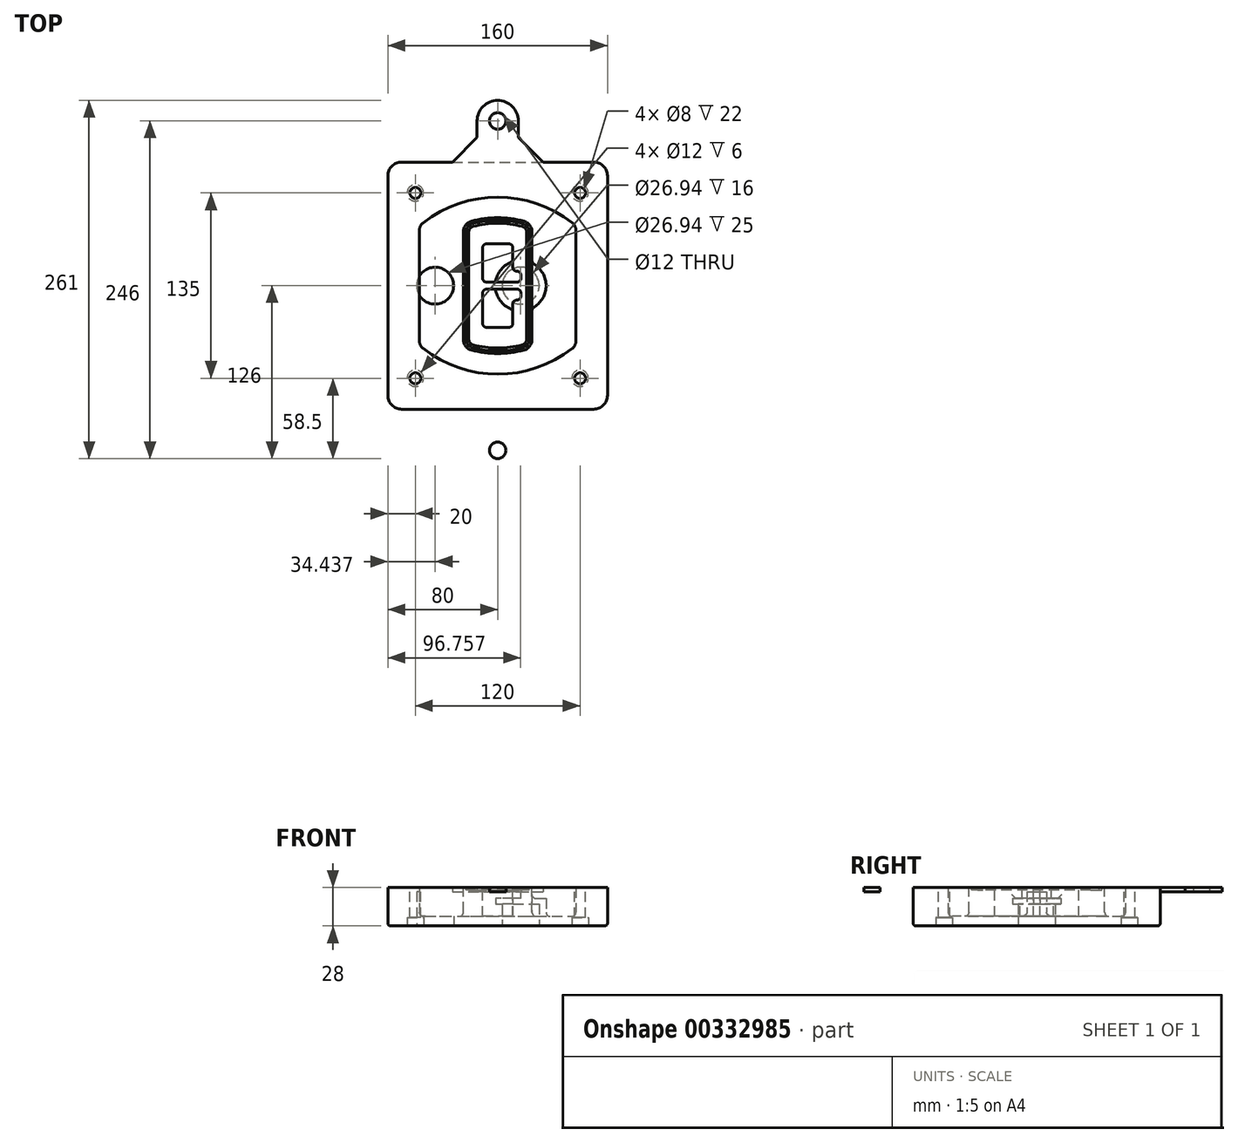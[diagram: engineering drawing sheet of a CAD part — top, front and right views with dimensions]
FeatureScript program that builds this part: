
annotation { "Feature Type Name" : "Feature", "Feature Type Description" : "" }
export const myFeature = defineFeature(function(context is Context, id is Id, definition is map)
    precondition{}
    {
        {
            var Q0;
            Q0=qCreatedBy(makeId("Top.planeOp"),FACE);
            var sketch = newSketch(context, id + "F0", { "sketchPlane" : qUnion([Q0])});
            skPoint(sketch, "E0.rect.middle", {"position": v(0, 0) * mm});
            skLineSegment(sketch, "E1.bottom", {"start": v(-70, -90) * mm, "end": v(70, -90) * mm});
            skLineSegment(sketch, "E1.top", {"start": v(-70, 90) * mm, "end": v(70, 90) * mm});
            skLineSegment(sketch, "E1.left", {"start": v(-80, -80) * mm, "end": v(-80, 80) * mm});
            skLineSegment(sketch, "E1.right", {"start": v(80, -80) * mm, "end": v(80, 80) * mm});
            skLineSegment(sketch, "E2", {"start": v(-80, 90) * mm, "end": v(80, -90) * mm, "construction": true});
            skLineSegment(sketch, "E3", {"start": v(80, 90) * mm, "end": v(-80, -90) * mm, "construction": true});
            skCircle(sketch, "E4", {"center": v(-60, 67.5) * mm, "radius": 4 * mm});
            skCircle(sketch, "E5", {"center": v(60, 67.5) * mm, "radius": 4 * mm});
            skCircle(sketch, "E6", {"center": v(60, -67.5) * mm, "radius": 4 * mm});
            skCircle(sketch, "E7", {"center": v(-60, -67.5) * mm, "radius": 4 * mm});
            skLineSegment(sketch, "E8", {"start": v(-60, 67.5) * mm, "end": v(60, 67.5) * mm, "construction": true});
            skLineSegment(sketch, "E9", {"start": v(60, 67.5) * mm, "end": v(60, -67.5) * mm, "construction": true});
            skLineSegment(sketch, "E10", {"start": v(60, -67.5) * mm, "end": v(-60, -67.5) * mm, "construction": true});
            skLineSegment(sketch, "E11", {"start": v(-60, -67.5) * mm, "end": v(-60, 67.5) * mm, "construction": true});
            skLineSegment(sketch, "E12", {"start": v(-60, 40.3) * mm, "end": v(-60, -40.3) * mm});
            skLineSegment(sketch, "E13", {"start": v(60, 40.3) * mm, "end": v(60, -40.3) * mm});
            skArc(sketch, "E14", {"start": v(56.15, 48.18) * mm, "mid": v(0, 67.5) * mm, "end": v(-56.15, 48.18) * mm});
            skArc(sketch, "E15", {"start": v(-56.15, -48.18) * mm, "mid": v(0, -67.5) * mm, "end": v(56.15, -48.18) * mm});
            skLineSegment(sketch, "E16", {"start": v(-60, 0) * mm, "end": v(60, 0) * mm, "construction": true});
            skPoint(sketch, "E17.visualSharp", {"position": v(-60, -45) * mm});
            skArc(sketch, "E17.filletArc", {"start": v(-60, -40.3) * mm, "mid": v(-58.99, -44.68) * mm, "end": v(-56.15, -48.18) * mm});
            skPoint(sketch, "E18.visualSharp", {"position": v(-60, 45) * mm});
            skArc(sketch, "E18.filletArc", {"start": v(-56.15, 48.18) * mm, "mid": v(-58.99, 44.68) * mm, "end": v(-60, 40.3) * mm});
            skPoint(sketch, "E19.visualSharp", {"position": v(60, 45) * mm});
            skArc(sketch, "E19.filletArc", {"start": v(60, 40.3) * mm, "mid": v(58.99, 44.68) * mm, "end": v(56.15, 48.18) * mm});
            skPoint(sketch, "E20.visualSharp", {"position": v(60, -45) * mm});
            skArc(sketch, "E20.filletArc", {"start": v(56.15, -48.18) * mm, "mid": v(58.99, -44.68) * mm, "end": v(60, -40.3) * mm});
            skPoint(sketch, "E21.visualSharp", {"position": v(-80, 90) * mm});
            skArc(sketch, "E21.filletArc", {"start": v(-70, 90) * mm, "mid": v(-77.07, 87.07) * mm, "end": v(-80, 80) * mm});
            skPoint(sketch, "E22.visualSharp", {"position": v(80, 90) * mm});
            skArc(sketch, "E22.filletArc", {"start": v(80, 80) * mm, "mid": v(77.07, 87.07) * mm, "end": v(70, 90) * mm});
            skPoint(sketch, "E23.visualSharp", {"position": v(80, -90) * mm});
            skArc(sketch, "E23.filletArc", {"start": v(70, -90) * mm, "mid": v(77.07, -87.07) * mm, "end": v(80, -80) * mm});
            skPoint(sketch, "E24.visualSharp", {"position": v(-80, -90) * mm});
            skArc(sketch, "E24.filletArc", {"start": v(-80, -80) * mm, "mid": v(-77.07, -87.07) * mm, "end": v(-70, -90) * mm});
            skArc(sketch, "E25.0", {"start": v(57, 40.3) * mm, "mid": v(56.3, 43.36) * mm, "end": v(54.3, 45.81) * mm});
            skLineSegment(sketch, "E25.1", {"start": v(57, 40.3) * mm, "end": v(57, -40.3) * mm});
            skArc(sketch, "E25.2", {"start": v(54.3, -45.81) * mm, "mid": v(56.3, -43.36) * mm, "end": v(57, -40.3) * mm});
            skArc(sketch, "E25.3", {"start": v(-54.3, -45.81) * mm, "mid": v(0, -64.5) * mm, "end": v(54.3, -45.81) * mm});
            skArc(sketch, "E25.4", {"start": v(-57, -40.3) * mm, "mid": v(-56.3, -43.36) * mm, "end": v(-54.3, -45.81) * mm});
            skArc(sketch, "E25.5", {"start": v(54.3, 45.81) * mm, "mid": v(0, 64.5) * mm, "end": v(-54.3, 45.81) * mm});
            skLineSegment(sketch, "E25.6", {"start": v(-57, 40.3) * mm, "end": v(-57, -40.3) * mm});
            skArc(sketch, "E25.7", {"start": v(-54.3, 45.81) * mm, "mid": v(-56.3, 43.36) * mm, "end": v(-57, 40.3) * mm});
            skArc(sketch, "E26.0", {"start": v(-58.62, 51.33) * mm, "mid": v(-62.58, 46.43) * mm, "end": v(-64, 40.3) * mm});
            skArc(sketch, "E26.1", {"start": v(58.62, 51.33) * mm, "mid": v(0, 71.5) * mm, "end": v(-58.62, 51.33) * mm});
            skArc(sketch, "E26.2", {"start": v(64, 40.3) * mm, "mid": v(62.58, 46.43) * mm, "end": v(58.62, 51.33) * mm});
            skLineSegment(sketch, "E26.3", {"start": v(64, 40.3) * mm, "end": v(64, -40.3) * mm});
            skArc(sketch, "E26.4", {"start": v(58.62, -51.33) * mm, "mid": v(62.58, -46.43) * mm, "end": v(64, -40.3) * mm});
            skLineSegment(sketch, "E26.5", {"start": v(-64, 40.3) * mm, "end": v(-64, -40.3) * mm});
            skArc(sketch, "E26.6", {"start": v(-58.62, -51.33) * mm, "mid": v(0, -71.5) * mm, "end": v(58.62, -51.33) * mm});
            skArc(sketch, "E26.7", {"start": v(-64, -40.3) * mm, "mid": v(-62.58, -46.43) * mm, "end": v(-58.62, -51.33) * mm});
            skSolve(sketch);
        }
        {
            var Q0;
            Q0=makeQuery(id+"F0.imprint","IMPRINT",FACE,{"disambiguationData":[TD([[makeQuery(id+"F0.imprint","IMPRINT",EDGE,{"derivedFrom":sQuery(id+"F0.wireOp",EDGE,"E1.bottom")}),1.0]])]});
            var Q1;
            Q1=makeQuery(id+"F0.imprint","IMPRINT",FACE,{"disambiguationData":[TD([[makeQuery(id+"F0.imprint","IMPRINT",EDGE,{"derivedFrom":sQuery(id+"F0.wireOp",EDGE,"E12")}),1.0]])]});
            var Q2;
            Q2=makeQuery(id+"F0.imprint","IMPRINT",FACE,{"disambiguationData":[TD([[makeQuery(id+"F0.imprint","IMPRINT",EDGE,{"derivedFrom":sQuery(id+"F0.wireOp",EDGE,"E25.0")}),1.0]])]});
            var Q3;
            Q3=makeQuery(id+"F0.imprint","IMPRINT",FACE,{"disambiguationData":[TD([[makeQuery(id+"F0.imprint","IMPRINT",EDGE,{"derivedFrom":sQuery(id+"F0.wireOp",EDGE,"E12")}),-1.0]])]});
            extrude(context, id + "F1", {"entities" : qUnion([Q0, Q1, Q2, Q3]), "oppositeDirection" : true, "depth" : 25 * mm});
        }
        {
            var Q0;
            Q0=makeQuery(id+"F0.imprint","IMPRINT",FACE,{"disambiguationData":[TD([[makeQuery(id+"F0.imprint","IMPRINT",EDGE,{"derivedFrom":sQuery(id+"F0.wireOp",EDGE,"E12")}),1.0]])]});
            extrude(context, id + "F2", {"entities" : qUnion([Q0]), "operationType" : NewBodyOperationType.ADD, "depth" : 3 * mm});
        }
        {
            var Q0;
            Q0=makeQuery(id+"F0.imprint","IMPRINT",FACE,{"disambiguationData":[TD([[makeQuery(id+"F0.imprint","IMPRINT",EDGE,{"derivedFrom":sQuery(id+"F0.wireOp",EDGE,"E25.0")}),1.0]])]});
            extrude(context, id + "F3", {"entities" : qUnion([Q0]), "operationType" : NewBodyOperationType.REMOVE, "oppositeDirection" : true, "depth" : 18 * mm});
        }
        {
            var Q0;
            Q0=makeQuery(id+"F2.opExtrude","CAP_FACE",FACE,{"disambiguationData":[OSD([sQuery(id+"F0.wireOp",EDGE,"E12"),sQuery(id+"F0.wireOp",EDGE,"E13"),sQuery(id+"F0.wireOp",EDGE,"E14"),sQuery(id+"F0.wireOp",EDGE,"E15"),sQuery(id+"F0.wireOp",EDGE,"E17.filletArc"),sQuery(id+"F0.wireOp",EDGE,"E18.filletArc"),sQuery(id+"F0.wireOp",EDGE,"E19.filletArc"),sQuery(id+"F0.wireOp",EDGE,"E20.filletArc"),sQuery(id+"F0.wireOp",EDGE,"E25.0"),sQuery(id+"F0.wireOp",EDGE,"E25.1"),sQuery(id+"F0.wireOp",EDGE,"E25.2"),sQuery(id+"F0.wireOp",EDGE,"E25.3"),sQuery(id+"F0.wireOp",EDGE,"E25.4"),sQuery(id+"F0.wireOp",EDGE,"E25.5"),sQuery(id+"F0.wireOp",EDGE,"E25.6"),sQuery(id+"F0.wireOp",EDGE,"E25.7")])],"isStart":false});
            var sketch = newSketch(context, id + "F4", { "sketchPlane" : qUnion([Q0])});
            skArc(sketch, "E27.0", {"start": v(-19.08, -46.97) * mm, "mid": v(0, -49.5) * mm, "end": v(19.08, -46.97) * mm});
            skArc(sketch, "E28.0", {"start": v(19.08, 46.97) * mm, "mid": v(0, 49.5) * mm, "end": v(-19.08, 46.97) * mm});
            skLineSegment(sketch, "E29", {"start": v(-25, 39.25) * mm, "end": v(-25, -39.25) * mm});
            skLineSegment(sketch, "E30", {"start": v(25, 39.25) * mm, "end": v(25, -39.25) * mm});
            skLineSegment(sketch, "E31", {"start": v(-25, 45.1) * mm, "end": v(25, 45.1) * mm, "construction": true});
            skLineSegment(sketch, "E32", {"start": v(-25, -45.1) * mm, "end": v(25, -45.1) * mm, "construction": true});
            skPoint(sketch, "E33.visualSharp", {"position": v(-25, 45.1) * mm});
            skArc(sketch, "E33.filletArc", {"start": v(-19.08, 46.97) * mm, "mid": v(-23.35, 44.11) * mm, "end": v(-25, 39.25) * mm});
            skPoint(sketch, "E34.visualSharp", {"position": v(25, 45.1) * mm});
            skArc(sketch, "E34.filletArc", {"start": v(25, 39.25) * mm, "mid": v(23.35, 44.11) * mm, "end": v(19.08, 46.97) * mm});
            skPoint(sketch, "E35.visualSharp", {"position": v(25, -45.1) * mm});
            skArc(sketch, "E35.filletArc", {"start": v(19.08, -46.97) * mm, "mid": v(23.35, -44.11) * mm, "end": v(25, -39.25) * mm});
            skPoint(sketch, "E36.visualSharp", {"position": v(-25, -45.1) * mm});
            skArc(sketch, "E36.filletArc", {"start": v(-25, -39.25) * mm, "mid": v(-23.35, -44.11) * mm, "end": v(-19.08, -46.97) * mm});
            skArc(sketch, "E37.0", {"start": v(54.3, 45.81) * mm, "mid": v(0, 64.5) * mm, "end": v(-54.3, 45.81) * mm});
            skArc(sketch, "E37.1", {"start": v(-54.3, 45.81) * mm, "mid": v(-56.3, 43.36) * mm, "end": v(-57, 40.3) * mm});
            skLineSegment(sketch, "E37.2", {"start": v(-57, 40.3) * mm, "end": v(-57, -40.3) * mm});
            skArc(sketch, "E37.3", {"start": v(-57, -40.3) * mm, "mid": v(-56.3, -43.36) * mm, "end": v(-54.3, -45.81) * mm});
            skArc(sketch, "E37.4", {"start": v(-54.3, -45.81) * mm, "mid": v(0, -64.5) * mm, "end": v(54.3, -45.81) * mm});
            skArc(sketch, "E37.5", {"start": v(54.3, -45.81) * mm, "mid": v(56.3, -43.36) * mm, "end": v(57, -40.3) * mm});
            skLineSegment(sketch, "E37.6", {"start": v(57, 40.3) * mm, "end": v(57, -40.3) * mm});
            skArc(sketch, "E37.7", {"start": v(57, 40.3) * mm, "mid": v(56.3, 43.36) * mm, "end": v(54.3, 45.81) * mm});
            skLineSegment(sketch, "E38.0", {"start": v(23, 39.25) * mm, "end": v(23, -39.25) * mm});
            skArc(sketch, "E38.1", {"start": v(18.56, -45.04) * mm, "mid": v(21.76, -42.9) * mm, "end": v(23, -39.25) * mm});
            skArc(sketch, "E38.2", {"start": v(-18.56, -45.04) * mm, "mid": v(0, -47.5) * mm, "end": v(18.56, -45.04) * mm});
            skArc(sketch, "E38.3", {"start": v(-23, -39.25) * mm, "mid": v(-21.76, -42.9) * mm, "end": v(-18.56, -45.04) * mm});
            skLineSegment(sketch, "E38.4", {"start": v(-23, 39.25) * mm, "end": v(-23, -39.25) * mm});
            skArc(sketch, "E38.5", {"start": v(23, 39.25) * mm, "mid": v(21.76, 42.9) * mm, "end": v(18.56, 45.04) * mm});
            skArc(sketch, "E38.6", {"start": v(-18.56, 45.04) * mm, "mid": v(-21.76, 42.9) * mm, "end": v(-23, 39.25) * mm});
            skArc(sketch, "E38.7", {"start": v(18.56, 45.04) * mm, "mid": v(0, 47.5) * mm, "end": v(-18.56, 45.04) * mm});
            skArc(sketch, "E39.0", {"start": v(21, 39.25) * mm, "mid": v(20.18, 41.68) * mm, "end": v(18.04, 43.1) * mm});
            skLineSegment(sketch, "E39.1", {"start": v(21, 39.25) * mm, "end": v(21, -39.25) * mm});
            skArc(sketch, "E39.2", {"start": v(18.04, -43.1) * mm, "mid": v(20.18, -41.68) * mm, "end": v(21, -39.25) * mm});
            skArc(sketch, "E39.3", {"start": v(-18.04, -43.1) * mm, "mid": v(0, -45.5) * mm, "end": v(18.04, -43.1) * mm});
            skArc(sketch, "E39.4", {"start": v(-21, -39.25) * mm, "mid": v(-20.18, -41.68) * mm, "end": v(-18.04, -43.1) * mm});
            skArc(sketch, "E39.5", {"start": v(18.04, 43.1) * mm, "mid": v(0, 45.5) * mm, "end": v(-18.04, 43.1) * mm});
            skLineSegment(sketch, "E39.6", {"start": v(-21, 39.25) * mm, "end": v(-21, -39.25) * mm});
            skArc(sketch, "E39.7", {"start": v(-18.04, 43.1) * mm, "mid": v(-20.18, 41.68) * mm, "end": v(-21, 39.25) * mm});
            skLineSegment(sketch, "E40", {"start": v(-25, 0) * mm, "end": v(25, 0) * mm, "construction": true});
            skLineSegment(sketch, "E41", {"start": v(-11, 5.5) * mm, "end": v(-11, 27.5) * mm});
            skLineSegment(sketch, "E42", {"start": v(-8, 30.5) * mm, "end": v(8, 30.5) * mm});
            skLineSegment(sketch, "E43", {"start": v(11, 27.5) * mm, "end": v(11, 13.5) * mm});
            skLineSegment(sketch, "E44", {"start": v(14, 10.5) * mm, "end": v(14, 10.5) * mm});
            skLineSegment(sketch, "E45", {"start": v(17, 7.5) * mm, "end": v(17, 5.5) * mm});
            skLineSegment(sketch, "E46", {"start": v(14, 2.5) * mm, "end": v(-8, 2.5) * mm});
            skPoint(sketch, "E47.visualSharp", {"position": v(-11, 30.5) * mm});
            skArc(sketch, "E47.filletArc", {"start": v(-8, 30.5) * mm, "mid": v(-10.12, 29.62) * mm, "end": v(-11, 27.5) * mm});
            skPoint(sketch, "E48.visualSharp", {"position": v(11, 30.5) * mm});
            skArc(sketch, "E48.filletArc", {"start": v(11, 27.5) * mm, "mid": v(10.12, 29.62) * mm, "end": v(8, 30.5) * mm});
            skPoint(sketch, "E49.visualSharp", {"position": v(11, 10.5) * mm});
            skArc(sketch, "E49.filletArc", {"start": v(11, 13.5) * mm, "mid": v(11.88, 11.38) * mm, "end": v(14, 10.5) * mm});
            skPoint(sketch, "E50.visualSharp", {"position": v(17, 10.5) * mm});
            skArc(sketch, "E50.filletArc", {"start": v(17, 7.5) * mm, "mid": v(16.12, 9.62) * mm, "end": v(14, 10.5) * mm});
            skPoint(sketch, "E51.visualSharp", {"position": v(17, 2.5) * mm});
            skArc(sketch, "E51.filletArc", {"start": v(14, 2.5) * mm, "mid": v(16.12, 3.38) * mm, "end": v(17, 5.5) * mm});
            skPoint(sketch, "E52.visualSharp", {"position": v(-11, 2.5) * mm});
            skArc(sketch, "E52.filletArc", {"start": v(-11, 5.5) * mm, "mid": v(-10.12, 3.38) * mm, "end": v(-8, 2.5) * mm});
            skLineSegment(sketch, "E53.0.MirrorCS", {"start": v(14, -2.5) * mm, "end": v(-8, -2.5) * mm});
            skArc(sketch, "E54.0.MirrorCS", {"start": v(-11, -5.5) * mm, "mid": v(-10.12, -3.38) * mm, "end": v(-8, -2.5) * mm});
            skLineSegment(sketch, "E55.0.MirrorCS", {"start": v(-11, -5.5) * mm, "end": v(-11, -27.5) * mm});
            skArc(sketch, "E56.0.MirrorCS", {"start": v(-8, -30.5) * mm, "mid": v(-10.12, -29.62) * mm, "end": v(-11, -27.5) * mm});
            skLineSegment(sketch, "E57.0.MirrorCS", {"start": v(-8, -30.5) * mm, "end": v(8, -30.5) * mm});
            skArc(sketch, "E58.0.MirrorCS", {"start": v(11, -27.5) * mm, "mid": v(10.12, -29.62) * mm, "end": v(8, -30.5) * mm});
            skLineSegment(sketch, "E59.0.MirrorCS", {"start": v(11, -27.5) * mm, "end": v(11, -13.5) * mm});
            skArc(sketch, "E60.0.MirrorCS", {"start": v(11, -13.5) * mm, "mid": v(11.88, -11.38) * mm, "end": v(14, -10.5) * mm});
            skArc(sketch, "E61.0.MirrorCS", {"start": v(17, -7.5) * mm, "mid": v(16.12, -9.62) * mm, "end": v(14, -10.5) * mm});
            skLineSegment(sketch, "E62.0.MirrorCS", {"start": v(17, -7.5) * mm, "end": v(17, -5.5) * mm});
            skArc(sketch, "E63.0.MirrorCS", {"start": v(14, -2.5) * mm, "mid": v(16.12, -3.38) * mm, "end": v(17, -5.5) * mm});
            skSolve(sketch);
        }
        {
            var Q0;
            Q0=makeQuery(id+"F4.imprint","IMPRINT",FACE,{"disambiguationData":[TD([[makeQuery(id+"F4.imprint","IMPRINT",EDGE,{"derivedFrom":sQuery(id+"F4.wireOp",EDGE,"E27.0")}),1.0]])]});
            var Q1;
            Q1=makeQuery(id+"F4.imprint","IMPRINT",FACE,{"disambiguationData":[TD([[makeQuery(id+"F4.imprint","IMPRINT",EDGE,{"derivedFrom":sQuery(id+"F4.wireOp",EDGE,"E38.0")}),-1.0]])]});
            var Q2;
            Q2=makeQuery(id+"F4.imprint","IMPRINT",FACE,{"disambiguationData":[TD([[makeQuery(id+"F4.imprint","IMPRINT",EDGE,{"derivedFrom":sQuery(id+"F4.wireOp",EDGE,"E39.0")}),1.0]])]});
            extrude(context, id + "F5", {"entities" : qUnion([Q0, Q1, Q2]), "operationType" : NewBodyOperationType.ADD, "endBound" : BoundingType.UP_TO_NEXT, "oppositeDirection" : true, "depth" : 25 * mm});
        }
        {
            var Q0;
            Q0=makeQuery(id+"F4.imprint","IMPRINT",FACE,{"disambiguationData":[TD([[makeQuery(id+"F4.imprint","IMPRINT",EDGE,{"derivedFrom":sQuery(id+"F4.wireOp",EDGE,"E38.0")}),-1.0]])]});
            extrude(context, id + "F6", {"entities" : qUnion([Q0]), "operationType" : NewBodyOperationType.REMOVE, "oppositeDirection" : true, "depth" : 2 * mm});
        }
        {
            var Q0;
            Q0=makeQuery(id+"F1.opExtrude","CAP_FACE",FACE,{"disambiguationData":[OSD([sQuery(id+"F0.wireOp",EDGE,"E1.bottom"),sQuery(id+"F0.wireOp",EDGE,"E1.top"),sQuery(id+"F0.wireOp",EDGE,"E1.left"),sQuery(id+"F0.wireOp",EDGE,"E1.right"),sQuery(id+"F0.wireOp",EDGE,"E4"),sQuery(id+"F0.wireOp",EDGE,"E5"),sQuery(id+"F0.wireOp",EDGE,"E6"),sQuery(id+"F0.wireOp",EDGE,"E7"),sQuery(id+"F0.wireOp",EDGE,"E21.filletArc"),sQuery(id+"F0.wireOp",EDGE,"E22.filletArc"),sQuery(id+"F0.wireOp",EDGE,"E23.filletArc"),sQuery(id+"F0.wireOp",EDGE,"E24.filletArc")])],"isStart":false});
            var sketch = newSketch(context, id + "F7", { "sketchPlane" : qUnion([Q0])});
            skCircle(sketch, "E64", {"center": v(16.76, 0) * mm, "radius": 13.47 * mm});
            skCircle(sketch, "E65", {"center": v(-45.56, 0) * mm, "radius": 13.47 * mm});
            skLineSegment(sketch, "E66", {"start": v(80, 0) * mm, "end": v(-80, 0) * mm});
            skCircle(sketch, "E67", {"center": v(16.76, 0) * mm, "radius": 18.47 * mm});
            skCircle(sketch, "E68", {"center": v(60, -67.5) * mm, "radius": 6 * mm});
            skCircle(sketch, "E69", {"center": v(-60, -67.5) * mm, "radius": 6 * mm});
            skCircle(sketch, "E70", {"center": v(-60, 67.5) * mm, "radius": 6 * mm});
            skCircle(sketch, "E71", {"center": v(60, 67.5) * mm, "radius": 6 * mm});
            skSolve(sketch);
        }
        {
            var Q0;
            {var subQ1=sQuery(id+"F7.wireOp",EDGE,"E66");var subQ4=sQuery(id+"F7.wireOp",EDGE,"E64");var subQ6=makeQuery(id+"F7.imprint","INTERSECT",VERTEX,{"disambiguationData":[OD(0.0)],"derivedFrom":[subQ4,subQ1]});Q0=makeQuery(id+"F7.imprint","IMPRINT",FACE,{"disambiguationData":[TD([[makeQuery(id+"F7.imprint","IMPRINT",EDGE,{"disambiguationData":[TD([[subQ6,-1.0]])],"derivedFrom":subQ4}),-1.0]])]});}
            var Q1;
            {var subQ0=sQuery(id+"F7.wireOp",EDGE,"E66");var subQ1=sQuery(id+"F7.wireOp",EDGE,"E64");var subQ3=makeQuery(id+"F7.imprint","INTERSECT",VERTEX,{"disambiguationData":[OD(0.0)],"derivedFrom":[subQ1,subQ0]});Q1=makeQuery(id+"F7.imprint","IMPRINT",FACE,{"disambiguationData":[TD([[makeQuery(id+"F7.imprint","IMPRINT",EDGE,{"disambiguationData":[TD([[subQ3,-1.0]])],"derivedFrom":subQ1}),1.0]])]});}
            var Q2;
            {var subQ0=sQuery(id+"F7.wireOp",EDGE,"E66");var subQ1=sQuery(id+"F7.wireOp",EDGE,"E64");var subQ3=makeQuery(id+"F7.imprint","INTERSECT",VERTEX,{"disambiguationData":[OD(0.0)],"derivedFrom":[subQ1,subQ0]});Q2=makeQuery(id+"F7.imprint","IMPRINT",FACE,{"disambiguationData":[TD([[makeQuery(id+"F7.imprint","IMPRINT",EDGE,{"disambiguationData":[TD([[subQ3,1.0]])],"derivedFrom":subQ1}),1.0]])]});}
            var Q3;
            {var subQ1=sQuery(id+"F7.wireOp",EDGE,"E66");var subQ4=sQuery(id+"F7.wireOp",EDGE,"E64");var subQ6=makeQuery(id+"F7.imprint","INTERSECT",VERTEX,{"disambiguationData":[OD(0.0)],"derivedFrom":[subQ4,subQ1]});Q3=makeQuery(id+"F7.imprint","IMPRINT",FACE,{"disambiguationData":[TD([[makeQuery(id+"F7.imprint","IMPRINT",EDGE,{"disambiguationData":[TD([[subQ6,1.0]])],"derivedFrom":subQ4}),-1.0]])]});}
            extrude(context, id + "F8", {"entities" : qUnion([Q0, Q1, Q2, Q3]), "operationType" : NewBodyOperationType.ADD, "oppositeDirection" : true, "depth" : 20 * mm});
        }
        {
            var Q0;
            {var subQ0=sQuery(id+"F7.wireOp",EDGE,"E66");var subQ1=sQuery(id+"F7.wireOp",EDGE,"E64");var subQ3=makeQuery(id+"F7.imprint","INTERSECT",VERTEX,{"disambiguationData":[OD(0.0)],"derivedFrom":[subQ1,subQ0]});Q0=makeQuery(id+"F7.imprint","IMPRINT",FACE,{"disambiguationData":[TD([[makeQuery(id+"F7.imprint","IMPRINT",EDGE,{"disambiguationData":[TD([[subQ3,-1.0]])],"derivedFrom":subQ1}),1.0]])]});}
            var Q1;
            {var subQ0=sQuery(id+"F7.wireOp",EDGE,"E66");var subQ1=sQuery(id+"F7.wireOp",EDGE,"E64");var subQ3=makeQuery(id+"F7.imprint","INTERSECT",VERTEX,{"disambiguationData":[OD(0.0)],"derivedFrom":[subQ1,subQ0]});Q1=makeQuery(id+"F7.imprint","IMPRINT",FACE,{"disambiguationData":[TD([[makeQuery(id+"F7.imprint","IMPRINT",EDGE,{"disambiguationData":[TD([[subQ3,1.0]])],"derivedFrom":subQ1}),1.0]])]});}
            extrude(context, id + "F9", {"entities" : qUnion([Q0, Q1]), "operationType" : NewBodyOperationType.REMOVE, "oppositeDirection" : true, "depth" : 16 * mm});
        }
        {
            var Q0;
            {var subQ0=sQuery(id+"F7.wireOp",EDGE,"E66");var subQ1=sQuery(id+"F7.wireOp",EDGE,"E65");var subQ3=makeQuery(id+"F7.imprint","INTERSECT",VERTEX,{"disambiguationData":[OD(0.0)],"derivedFrom":[subQ1,subQ0]});Q0=makeQuery(id+"F7.imprint","IMPRINT",FACE,{"disambiguationData":[TD([[makeQuery(id+"F7.imprint","IMPRINT",EDGE,{"disambiguationData":[TD([[subQ3,-1.0]])],"derivedFrom":subQ1}),1.0]])]});}
            var Q1;
            {var subQ0=sQuery(id+"F7.wireOp",EDGE,"E66");var subQ1=sQuery(id+"F7.wireOp",EDGE,"E65");var subQ3=makeQuery(id+"F7.imprint","INTERSECT",VERTEX,{"disambiguationData":[OD(0.0)],"derivedFrom":[subQ1,subQ0]});Q1=makeQuery(id+"F7.imprint","IMPRINT",FACE,{"disambiguationData":[TD([[makeQuery(id+"F7.imprint","IMPRINT",EDGE,{"disambiguationData":[TD([[subQ3,1.0]])],"derivedFrom":subQ1}),1.0]])]});}
            extrude(context, id + "F10", {"entities" : qUnion([Q0, Q1]), "operationType" : NewBodyOperationType.REMOVE, "oppositeDirection" : true, "depth" : 25 * mm});
        }
        {
            var Q0;
            Q0=makeQuery(id+"F7.imprint","IMPRINT",FACE,{"disambiguationData":[TD([[makeQuery(id+"F7.imprint","IMPRINT",EDGE,{"derivedFrom":sQuery(id+"F7.wireOp",EDGE,"E68")}),1.0]])]});
            var Q1;
            Q1=makeQuery(id+"F7.imprint","IMPRINT",FACE,{"disambiguationData":[TD([[makeQuery(id+"F7.imprint","IMPRINT",EDGE,{"derivedFrom":makeQuery(id+"F1.opExtrude","CAP_EDGE",EDGE,{"disambiguationData":[OSD([sQuery(id+"F0.wireOp",EDGE,"E5")])],"isStart":false})}),-1.0]])]});
            var Q2;
            Q2=makeQuery(id+"F7.imprint","IMPRINT",FACE,{"disambiguationData":[TD([[makeQuery(id+"F7.imprint","IMPRINT",EDGE,{"derivedFrom":sQuery(id+"F7.wireOp",EDGE,"E69")}),1.0]])]});
            var Q3;
            Q3=makeQuery(id+"F7.imprint","IMPRINT",FACE,{"disambiguationData":[TD([[makeQuery(id+"F7.imprint","IMPRINT",EDGE,{"derivedFrom":makeQuery(id+"F1.opExtrude","CAP_EDGE",EDGE,{"disambiguationData":[OSD([sQuery(id+"F0.wireOp",EDGE,"E4")])],"isStart":false})}),-1.0]])]});
            var Q4;
            Q4=makeQuery(id+"F7.imprint","IMPRINT",FACE,{"disambiguationData":[TD([[makeQuery(id+"F7.imprint","IMPRINT",EDGE,{"derivedFrom":sQuery(id+"F7.wireOp",EDGE,"E70")}),1.0]])]});
            var Q5;
            Q5=makeQuery(id+"F7.imprint","IMPRINT",FACE,{"disambiguationData":[TD([[makeQuery(id+"F7.imprint","IMPRINT",EDGE,{"derivedFrom":makeQuery(id+"F1.opExtrude","CAP_EDGE",EDGE,{"disambiguationData":[OSD([sQuery(id+"F0.wireOp",EDGE,"E7")])],"isStart":false})}),-1.0]])]});
            var Q6;
            Q6=makeQuery(id+"F7.imprint","IMPRINT",FACE,{"disambiguationData":[TD([[makeQuery(id+"F7.imprint","IMPRINT",EDGE,{"derivedFrom":sQuery(id+"F7.wireOp",EDGE,"E71")}),1.0]])]});
            var Q7;
            Q7=makeQuery(id+"F7.imprint","IMPRINT",FACE,{"disambiguationData":[TD([[makeQuery(id+"F7.imprint","IMPRINT",EDGE,{"derivedFrom":makeQuery(id+"F1.opExtrude","CAP_EDGE",EDGE,{"disambiguationData":[OSD([sQuery(id+"F0.wireOp",EDGE,"E6")])],"isStart":false})}),-1.0]])]});
            extrude(context, id + "F11", {"entities" : qUnion([Q0, Q1, Q2, Q3, Q4, Q5, Q6, Q7]), "operationType" : NewBodyOperationType.REMOVE, "oppositeDirection" : true, "depth" : 6 * mm});
        }
        {
            var Q0;
            Q0=makeQuery(id+"F9.boolean.opBoolean","COPY",FACE,{"derivedFrom":makeQuery(id+"F9.opExtrude","CAP_FACE",FACE,{"disambiguationData":[OSD([sQuery(id+"F7.wireOp",EDGE,"E64")])],"isStart":false})});
            var sketch = newSketch(context, id + "F12", { "sketchPlane" : qUnion([Q0])});
            skArc(sketch, "E72.0", {"start": v(11, 17.55) * mm, "mid": v(2.57, 11.82) * mm, "end": v(-1.54, 2.5) * mm});
            skArc(sketch, "E72.1", {"start": v(-1.54, -2.5) * mm, "mid": v(2.57, -11.82) * mm, "end": v(11, -17.55) * mm});
            skLineSegment(sketch, "E73", {"start": v(-1.54, -2.5) * mm, "end": v(14, -2.5) * mm});
            skLineSegment(sketch, "E74.0", {"start": v(14, 2.5) * mm, "end": v(-1.54, 2.5) * mm});
            skArc(sketch, "E74.1", {"start": v(14, 2.5) * mm, "mid": v(16.12, 3.38) * mm, "end": v(17, 5.5) * mm});
            skLineSegment(sketch, "E74.2", {"start": v(17, 7.5) * mm, "end": v(17, 5.5) * mm});
            skArc(sketch, "E74.3", {"start": v(17, 7.5) * mm, "mid": v(16.12, 9.62) * mm, "end": v(14, 10.5) * mm});
            skArc(sketch, "E74.4", {"start": v(11, 13.5) * mm, "mid": v(11.88, 11.38) * mm, "end": v(14, 10.5) * mm});
            skLineSegment(sketch, "E74.5", {"start": v(11, 17.55) * mm, "end": v(11, 13.5) * mm});
            skLineSegment(sketch, "E74.7", {"start": v(14, -2.5) * mm, "end": v(-1.54, -2.5) * mm});
            skArc(sketch, "E74.8", {"start": v(14, -2.5) * mm, "mid": v(16.12, -3.38) * mm, "end": v(17, -5.5) * mm});
            skLineSegment(sketch, "E74.9", {"start": v(17, -7.5) * mm, "end": v(17, -5.5) * mm});
            skArc(sketch, "E74.10", {"start": v(17, -7.5) * mm, "mid": v(16.12, -9.62) * mm, "end": v(14, -10.5) * mm});
            skArc(sketch, "E74.11", {"start": v(11, -13.5) * mm, "mid": v(11.88, -11.38) * mm, "end": v(14, -10.5) * mm});
            skLineSegment(sketch, "E74.12", {"start": v(11, -17.55) * mm, "end": v(11, -13.5) * mm});
            skPoint(sketch, "E75.orphan", {"position": v(11, -27.5) * mm});
            skPoint(sketch, "E76.orphan", {"position": v(-8, -2.5) * mm});
            skPoint(sketch, "E77.orphan", {"position": v(-8, 2.5) * mm});
            skPoint(sketch, "E78.orphan", {"position": v(11, 27.5) * mm});
            skSolve(sketch);
        }
        {
            var Q0;
            {var subQ7=sQuery(id+"F12.wireOp",EDGE,"E72.0");var subQ14=sQuery(id+"F12.wireOp",EDGE,"E72.1");var subQ16=sQuery(id+"F12.wireOp",EDGE,"E74.1");var subQ18=sQuery(id+"F12.wireOp",EDGE,"E74.8");Q0=qUnion([makeQuery(id+"F12.imprint","IMPRINT",FACE,{"disambiguationData":[TD([[makeQuery(id+"F12.imprint","IMPRINT",EDGE,{"derivedFrom":subQ7}),1.0]])]}),makeQuery(id+"F12.imprint","IMPRINT",FACE,{"disambiguationData":[TD([[makeQuery(id+"F12.imprint","IMPRINT",EDGE,{"derivedFrom":subQ14}),1.0]])]}),makeQuery(id+"F12.imprint","IMPRINT",FACE,{"disambiguationData":[TD([[makeQuery(id+"F12.imprint","IMPRINT",EDGE,{"derivedFrom":subQ16}),1.0]])]}),makeQuery(id+"F12.imprint","IMPRINT",FACE,{"disambiguationData":[TD([[makeQuery(id+"F12.imprint","IMPRINT",EDGE,{"derivedFrom":subQ18}),-1.0]])]})]);}
            var Q1;
            Q1=makeQuery(id+"F5.boolean.opBoolean","SPLIT",FACE,{"disambiguationData":[TD([makeQuery(id+"F5.opExtrude","SWEPT_FACE",FACE,{"disambiguationData":[OSD([sQuery(id+"F4.wireOp",EDGE,"E41")])]})])],"derivedFrom":makeQuery(id+"F3.boolean.opBoolean","COPY",FACE,{"derivedFrom":makeQuery(id+"F3.opExtrude","CAP_FACE",FACE,{"disambiguationData":[OSD([sQuery(id+"F0.wireOp",EDGE,"E25.0"),sQuery(id+"F0.wireOp",EDGE,"E25.1"),sQuery(id+"F0.wireOp",EDGE,"E25.2"),sQuery(id+"F0.wireOp",EDGE,"E25.3"),sQuery(id+"F0.wireOp",EDGE,"E25.4"),sQuery(id+"F0.wireOp",EDGE,"E25.5"),sQuery(id+"F0.wireOp",EDGE,"E25.6"),sQuery(id+"F0.wireOp",EDGE,"E25.7")])],"isStart":false})})});
            extrude(context, id + "F13", {"entities" : qUnion([Q0]), "operationType" : NewBodyOperationType.REMOVE, "endBound" : BoundingType.UP_TO_SURFACE, "endBoundEntityFace" : qUnion([Q1]), "depth" : 25 * mm});
        }
        {
            var Q0;
            Q0=makeQuery(id+"F3.boolean.opBoolean","COPY",EDGE,{"derivedFrom":makeQuery(id+"F3.opExtrude","CAP_EDGE",EDGE,{"disambiguationData":[OSD([sQuery(id+"F0.wireOp",EDGE,"E25.6")])],"isStart":false})});
            var Q1;
            Q1=makeQuery(id+"F8.boolean.opBoolean","INTERSECT",EDGE,{"derivedFrom":[makeQuery(id+"F5.opExtrude","SWEPT_FACE",FACE,{"disambiguationData":[OSD([sQuery(id+"F4.wireOp",EDGE,"E30")])]}),makeQuery(id+"F8.opExtrude","CAP_FACE",FACE,{"disambiguationData":[OSD([sQuery(id+"F7.wireOp",EDGE,"E67")])],"isStart":false})]});
            var Q2;
            Q2=makeQuery(id+"F8.boolean.opBoolean","INTERSECT",EDGE,{"disambiguationData":[OD(1.0)],"derivedFrom":[makeQuery(id+"F5.opExtrude","SWEPT_FACE",FACE,{"disambiguationData":[OSD([sQuery(id+"F4.wireOp",EDGE,"E30")])]}),makeQuery(id+"F8.opExtrude","SWEPT_FACE",FACE,{"disambiguationData":[OSD([sQuery(id+"F7.wireOp",EDGE,"E67")])]})]});
            var Q3;
            {var subQ0=sQuery(id+"F4.wireOp",EDGE,"E30");Q3=makeQuery(id+"F8.boolean.opBoolean","SPLIT",EDGE,{"disambiguationData":[TD([makeQuery(id+"F5.opExtrude","SWEPT_FACE",FACE,{"disambiguationData":[OSD([sQuery(id+"F4.wireOp",EDGE,"E35.filletArc")])]})])],"derivedFrom":makeQuery(id+"F5.opExtrude","CAP_EDGE",EDGE,{"disambiguationData":[OSD([subQ0])],"isStart":false})});}
            var Q4;
            {var subQ0=sQuery(id+"F0.wireOp",EDGE,"E25.7");var subQ1=sQuery(id+"F0.wireOp",EDGE,"E25.1");var subQ2=sQuery(id+"F0.wireOp",EDGE,"E25.6");var subQ3=sQuery(id+"F0.wireOp",EDGE,"E25.5");var subQ4=sQuery(id+"F0.wireOp",EDGE,"E25.4");var subQ5=sQuery(id+"F0.wireOp",EDGE,"E25.0");var subQ6=sQuery(id+"F0.wireOp",EDGE,"E25.2");var subQ7=sQuery(id+"F0.wireOp",EDGE,"E25.3");Q4=makeQuery(id+"F8.boolean.opBoolean","INTERSECT",EDGE,{"derivedFrom":[makeQuery(id+"F5.boolean.opBoolean","SPLIT",FACE,{"disambiguationData":[TD([makeQuery(id+"F2.opExtrude","SWEPT_FACE",FACE,{"disambiguationData":[OSD([subQ5])]})])],"derivedFrom":makeQuery(id+"F3.boolean.opBoolean","COPY",FACE,{"derivedFrom":makeQuery(id+"F3.opExtrude","CAP_FACE",FACE,{"disambiguationData":[OSD([subQ5,subQ1,subQ6,subQ7,subQ4,subQ3,subQ2,subQ0])],"isStart":false})})}),makeQuery(id+"F8.opExtrude","SWEPT_FACE",FACE,{"disambiguationData":[OSD([sQuery(id+"F7.wireOp",EDGE,"E67")])]})]});}
            var Q5;
            Q5=makeQuery(id+"F8.boolean.opBoolean","INTERSECT",EDGE,{"disambiguationData":[OD(0.0)],"derivedFrom":[makeQuery(id+"F5.opExtrude","SWEPT_FACE",FACE,{"disambiguationData":[OSD([sQuery(id+"F4.wireOp",EDGE,"E30")])]}),makeQuery(id+"F8.opExtrude","SWEPT_FACE",FACE,{"disambiguationData":[OSD([sQuery(id+"F7.wireOp",EDGE,"E67")])]})]});
            fillet(context, id + "F14", {"entities" : qUnion([Q0, Q1, Q2, Q3, Q4, Q5]), "radius" : 3 * mm, "tangentPropagation" : true, "allowEdgeOverflow" : false});
        }
        {
            var Q0;
            Q0=makeQuery(id+"F1.opExtrude","CAP_EDGE",EDGE,{"disambiguationData":[OSD([sQuery(id+"F0.wireOp",EDGE,"E1.bottom")])],"isStart":false});
            fillet(context, id + "F15", {"entities" : qUnion([Q0]), "radius" : 2 * mm, "tangentPropagation" : true, "allowEdgeOverflow" : false});
        }
        {
            var Q0;
            {var subQ0=sQuery(id+"F0.wireOp",EDGE,"E21.filletArc");var subQ1=sQuery(id+"F0.wireOp",EDGE,"E7");var subQ2=sQuery(id+"F0.wireOp",EDGE,"E6");var subQ3=sQuery(id+"F0.wireOp",EDGE,"E5");var subQ4=sQuery(id+"F0.wireOp",EDGE,"E4");var subQ5=sQuery(id+"F0.wireOp",EDGE,"E22.filletArc");var subQ6=sQuery(id+"F0.wireOp",EDGE,"E1.bottom");var subQ7=sQuery(id+"F0.wireOp",EDGE,"E1.right");var subQ8=sQuery(id+"F0.wireOp",EDGE,"E1.top");var subQ9=sQuery(id+"F0.wireOp",EDGE,"E1.left");var subQ10=sQuery(id+"F0.wireOp",EDGE,"E23.filletArc");var subQ11=sQuery(id+"F0.wireOp",EDGE,"E24.filletArc");Q0=makeQuery(id+"F2.boolean.opBoolean","SPLIT",FACE,{"disambiguationData":[TD([makeQuery(id+"F1.opExtrude","SWEPT_FACE",FACE,{"disambiguationData":[OSD([subQ6])]})])],"derivedFrom":makeQuery(id+"F1.opExtrude","CAP_FACE",FACE,{"disambiguationData":[OSD([subQ6,subQ8,subQ9,subQ7,subQ4,subQ3,subQ2,subQ1,subQ0,subQ5,subQ10,subQ11])],"isStart":true})});}
            var sketch = newSketch(context, id + "F16", { "sketchPlane" : qUnion([Q0])});
            skLineSegment(sketch, "E79", {"start": v(0, 90) * mm, "end": v(0, 120) * mm, "construction": true});
            skCircle(sketch, "E80", {"center": v(0, 120) * mm, "radius": 6 * mm});
            skLineSegment(sketch, "E81", {"start": v(-33, 90) * mm, "end": v(-15, 108) * mm});
            skLineSegment(sketch, "E82", {"start": v(-15, 120) * mm, "end": v(-15, 108) * mm});
            skLineSegment(sketch, "E83", {"start": v(15, 108) * mm, "end": v(33, 90) * mm});
            skLineSegment(sketch, "E84", {"start": v(15, 108) * mm, "end": v(15, 120) * mm});
            skArc(sketch, "E85", {"start": v(15, 120) * mm, "mid": v(0, 135) * mm, "end": v(-15, 120) * mm});
            skLineSegment(sketch, "E86", {"start": v(-80, 0) * mm, "end": v(80, 0) * mm, "construction": true});
            skLineSegment(sketch, "E87.MirrorCS", {"start": v(15, -108) * mm, "end": v(33, -90) * mm});
            skLineSegment(sketch, "E88.MirrorCS", {"start": v(15, -108) * mm, "end": v(15, -120) * mm});
            skArc(sketch, "E89.MirrorCS", {"start": v(15, -120) * mm, "mid": v(0, -135) * mm, "end": v(-15, -120) * mm});
            skLineSegment(sketch, "E90.MirrorCS", {"start": v(-15, -120) * mm, "end": v(-15, -108) * mm});
            skLineSegment(sketch, "E91.MirrorCS", {"start": v(-33, -90) * mm, "end": v(-15, -108) * mm});
            skCircle(sketch, "E92.MirrorC", {"center": v(0, -120) * mm, "radius": 6 * mm});
            skLineSegment(sketch, "E93.MirrorCS", {"start": v(0, -90) * mm, "end": v(0, -120) * mm, "construction": true});
            skSolve(sketch);
        }
        {
            var Q0;
            Q0=makeQuery(id+"F16.imprint","IMPRINT",FACE,{"disambiguationData":[TD([[makeQuery(id+"F16.imprint","IMPRINT",EDGE,{"derivedFrom":makeQuery(id+"F1.opExtrude","CAP_EDGE",EDGE,{"disambiguationData":[OSD([sQuery(id+"F0.wireOp",EDGE,"E1.left")])],"isStart":true})}),-1.0]])]});
            var Q1;
            Q1=makeQuery(id+"F16.imprint","IMPRINT",FACE,{"disambiguationData":[TD([[makeQuery(id+"F16.imprint","IMPRINT",EDGE,{"derivedFrom":sQuery(id+"F16.wireOp",EDGE,"E92.MirrorC")}),1.0]])]});
            var Q2;
            Q2=makeQuery(id+"F16.imprint","IMPRINT",FACE,{"disambiguationData":[TD([[makeQuery(id+"F16.imprint","IMPRINT",EDGE,{"derivedFrom":sQuery(id+"F16.wireOp",EDGE,"E84")}),1.0]])]});
            var Q3;
            Q3=makeQuery(id+"F2.opExtrude","CAP_FACE",FACE,{"disambiguationData":[OSD([sQuery(id+"F0.wireOp",EDGE,"E12"),sQuery(id+"F0.wireOp",EDGE,"E13"),sQuery(id+"F0.wireOp",EDGE,"E14"),sQuery(id+"F0.wireOp",EDGE,"E15"),sQuery(id+"F0.wireOp",EDGE,"E17.filletArc"),sQuery(id+"F0.wireOp",EDGE,"E18.filletArc"),sQuery(id+"F0.wireOp",EDGE,"E19.filletArc"),sQuery(id+"F0.wireOp",EDGE,"E20.filletArc"),sQuery(id+"F0.wireOp",EDGE,"E25.0"),sQuery(id+"F0.wireOp",EDGE,"E25.1"),sQuery(id+"F0.wireOp",EDGE,"E25.2"),sQuery(id+"F0.wireOp",EDGE,"E25.3"),sQuery(id+"F0.wireOp",EDGE,"E25.4"),sQuery(id+"F0.wireOp",EDGE,"E25.5"),sQuery(id+"F0.wireOp",EDGE,"E25.6"),sQuery(id+"F0.wireOp",EDGE,"E25.7")])],"isStart":false});
            extrude(context, id + "F17", {"entities" : qUnion([Q0, Q1, Q2]), "operationType" : NewBodyOperationType.ADD, "endBound" : BoundingType.UP_TO_SURFACE, "endBoundEntityFace" : qUnion([Q3]), "depth" : 25 * mm});
        }
    });
